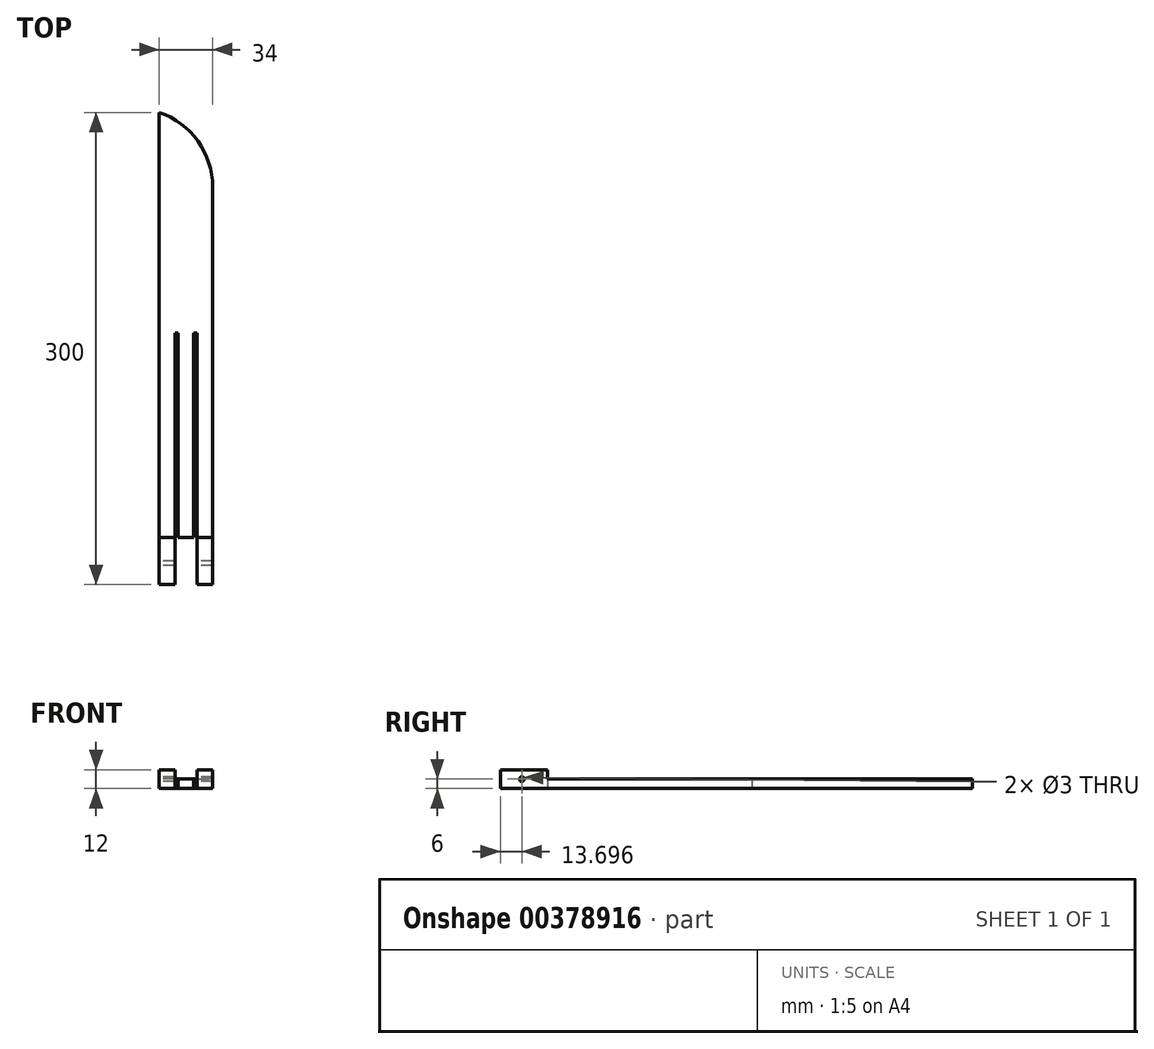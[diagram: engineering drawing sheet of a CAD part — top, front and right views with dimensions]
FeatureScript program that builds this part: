
annotation { "Feature Type Name" : "Feature", "Feature Type Description" : "" }
export const myFeature = defineFeature(function(context is Context, id is Id, definition is map)
    precondition{}
    {
        {
            var Q0;
            Q0=qCreatedBy(makeId("Top.planeOp"),FACE);
            var sketch = newSketch(context, id + "F0", { "sketchPlane" : qUnion([Q0])});
            skLineSegment(sketch, "E0.bottom", {"start": v(17, -150) * mm, "end": v(7, -150) * mm});
            skLineSegment(sketch, "E0.top", {"start": v(17, 150) * mm, "end": v(-17, 150) * mm});
            skLineSegment(sketch, "E0.left", {"start": v(17, -150) * mm, "end": v(17, 150) * mm});
            skLineSegment(sketch, "E0.right", {"start": v(-17, -150) * mm, "end": v(-17, 150) * mm});
            skPoint(sketch, "E0.middle", {"position": v(0, 0) * mm});
            skLineSegment(sketch, "E1.top", {"start": v(-7, 10) * mm, "end": v(-5, 10) * mm});
            skLineSegment(sketch, "E1.left", {"start": v(-7, -150) * mm, "end": v(-7, 10) * mm});
            skLineSegment(sketch, "E1.right", {"start": v(-5, -120) * mm, "end": v(-5, 10) * mm});
            skLineSegment(sketch, "E2.top", {"start": v(5, 10) * mm, "end": v(7, 10) * mm});
            skLineSegment(sketch, "E2.left", {"start": v(5, -120) * mm, "end": v(5, 10) * mm});
            skLineSegment(sketch, "E2.right", {"start": v(7, -150) * mm, "end": v(7, 10) * mm});
            skLineSegment(sketch, "E3.trimOffspring", {"start": v(-7, -150) * mm, "end": v(-17, -150) * mm});
            skLineSegment(sketch, "E4.top", {"start": v(-5, -120) * mm, "end": v(5, -120) * mm});
            skSolve(sketch);
        }
        {
            var Q0;
            Q0=makeQuery(id+"F0.imprint","IMPRINT",FACE,{"disambiguationData":[TD([[makeQuery(id+"F0.imprint","IMPRINT",EDGE,{"derivedFrom":sQuery(id+"F0.wireOp",EDGE,"E0.bottom")}),-1.0]])]});
            extrude(context, id + "F1", {"entities" : qUnion([Q0]), "depth" : 6 * mm});
        }
        {
            var Q0;
            Q0=makeQuery(id+"F1.opExtrude","CAP_FACE",FACE,{"disambiguationData":[OSD([sQuery(id+"F0.wireOp",EDGE,"E0.bottom"),sQuery(id+"F0.wireOp",EDGE,"E0.top"),sQuery(id+"F0.wireOp",EDGE,"E0.left"),sQuery(id+"F0.wireOp",EDGE,"E0.right"),sQuery(id+"F0.wireOp",EDGE,"E1.top"),sQuery(id+"F0.wireOp",EDGE,"E1.left"),sQuery(id+"F0.wireOp",EDGE,"E1.right"),sQuery(id+"F0.wireOp",EDGE,"E2.top"),sQuery(id+"F0.wireOp",EDGE,"E2.left"),sQuery(id+"F0.wireOp",EDGE,"E2.right"),sQuery(id+"F0.wireOp",EDGE,"E3.trimOffspring"),sQuery(id+"F0.wireOp",EDGE,"E4.top")])],"isStart":false});
            var sketch = newSketch(context, id + "F2", { "sketchPlane" : qUnion([Q0])});
            skLineSegment(sketch, "E5.bottom", {"start": v(-7, -120) * mm, "end": v(-17, -120) * mm});
            skLineSegment(sketch, "E5.top", {"start": v(-7, -150) * mm, "end": v(-17, -150) * mm});
            skLineSegment(sketch, "E5.left", {"start": v(-7, -120) * mm, "end": v(-7, -150) * mm});
            skLineSegment(sketch, "E5.right", {"start": v(-17, -120) * mm, "end": v(-17, -150) * mm});
            skLineSegment(sketch, "E6.bottom", {"start": v(7, -120) * mm, "end": v(17, -120) * mm});
            skLineSegment(sketch, "E6.top", {"start": v(7, -150) * mm, "end": v(17, -150) * mm});
            skLineSegment(sketch, "E6.left", {"start": v(7, -120) * mm, "end": v(7, -150) * mm});
            skLineSegment(sketch, "E6.right", {"start": v(17, -120) * mm, "end": v(17, -150) * mm});
            skSolve(sketch);
        }
        {
            var Q0;
            Q0=makeQuery(id+"F2.imprint","IMPRINT",FACE,{"disambiguationData":[TD([[makeQuery(id+"F2.imprint","IMPRINT",EDGE,{"derivedFrom":sQuery(id+"F2.wireOp",EDGE,"E5.bottom")}),1.0]])]});
            var Q1;
            Q1=makeQuery(id+"F2.imprint","IMPRINT",FACE,{"disambiguationData":[TD([[makeQuery(id+"F2.imprint","IMPRINT",EDGE,{"derivedFrom":sQuery(id+"F2.wireOp",EDGE,"E6.bottom")}),-1.0]])]});
            extrude(context, id + "F3", {"entities" : qUnion([Q0, Q1]), "operationType" : NewBodyOperationType.ADD, "depth" : 6 * mm});
        }
        {
            var Q0;
            Q0=makeQuery(id+"F3.boolean.opBoolean","MERGE",FACE,{"derivedFrom":[makeQuery(id+"F1.opExtrude","SWEPT_FACE",FACE,{"disambiguationData":[OSD([sQuery(id+"F0.wireOp",EDGE,"E0.right")])]}),makeQuery(id+"F3.opExtrude","SWEPT_FACE",FACE,{"disambiguationData":[OSD([sQuery(id+"F2.wireOp",EDGE,"E5.right")])]})]});
            var sketch = newSketch(context, id + "F4", { "sketchPlane" : qUnion([Q0])});
            skCircle(sketch, "E7", {"center": v(136.3, 6) * mm, "radius": 1.5 * mm});
            skPoint(sketch, "E7.centerSnap0", {"position": v(150, 6) * mm});
            skSolve(sketch);
        }
        {
            var Q0;
            Q0=makeQuery(id+"F4.imprint","IMPRINT",FACE,{"disambiguationData":[TD([[makeQuery(id+"F4.imprint","IMPRINT",EDGE,{"derivedFrom":sQuery(id+"F4.wireOp",EDGE,"E7")}),1.0]])]});
            extrude(context, id + "F5", {"entities" : qUnion([Q0]), "operationType" : NewBodyOperationType.REMOVE, "endBound" : BoundingType.THROUGH_ALL, "oppositeDirection" : true, "depth" : 25 * mm});
        }
        {
            var Q0;
            Q0=makeQuery(id+"F1.opExtrude","SWEPT_EDGE",EDGE,{"disambiguationData":[OSD([sQuery(id+"F0.wireOp",EDGE,"E0.top"),sQuery(id+"F0.wireOp",EDGE,"E0.left")])]});
            fillet(context, id + "F6", {"entities" : qUnion([Q0]), "radius" : 50 * mm, "tangentPropagation" : true, "allowEdgeOverflow" : false});
        }
    });
